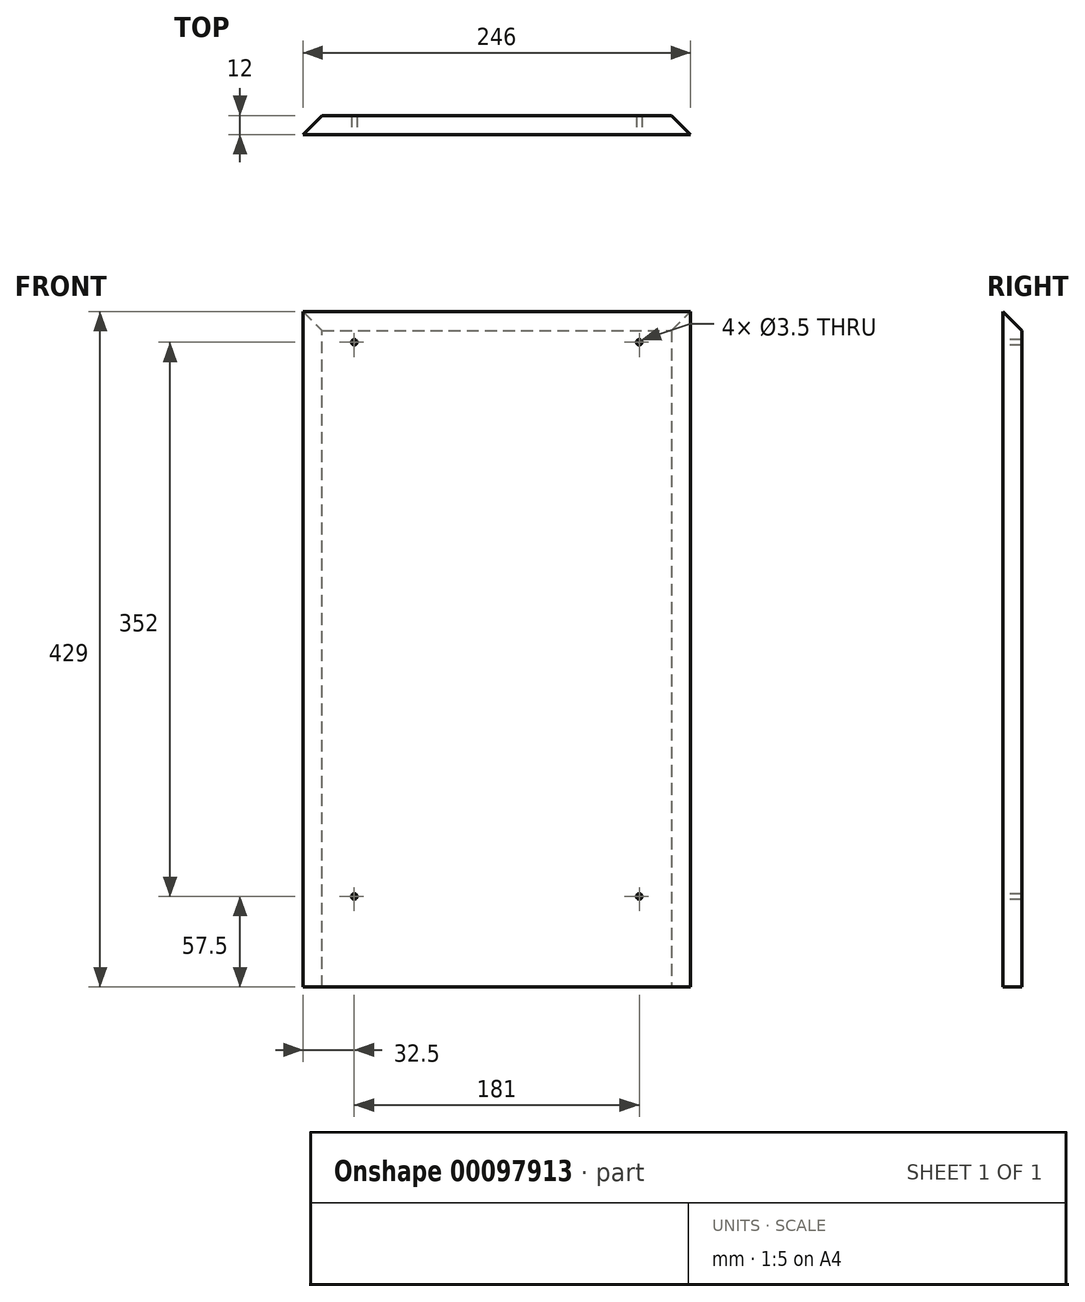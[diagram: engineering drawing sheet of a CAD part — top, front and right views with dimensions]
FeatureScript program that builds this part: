
annotation { "Feature Type Name" : "Feature", "Feature Type Description" : "" }
export const myFeature = defineFeature(function(context is Context, id is Id, definition is map)
    precondition{}
    {
        {
            var Q0;
            Q0=qCreatedBy(makeId("Front.planeOp"),FACE);
            var sketch = newSketch(context, id + "F0", { "sketchPlane" : qUnion([Q0])});
            skLineSegment(sketch, "E0.bottom", {"start": v(-123, 214.5) * mm, "end": v(123, 214.5) * mm});
            skLineSegment(sketch, "E0.top", {"start": v(-123, -214.5) * mm, "end": v(123, -214.5) * mm});
            skLineSegment(sketch, "E0.left", {"start": v(-123, 214.5) * mm, "end": v(-123, -214.5) * mm});
            skLineSegment(sketch, "E0.right", {"start": v(123, 214.5) * mm, "end": v(123, -214.5) * mm});
            skSolve(sketch);
        }
        {
            var Q0;
            Q0=makeQuery(id+"F0.imprint","IMPRINT",FACE,{"disambiguationData":[TD([[makeQuery(id+"F0.imprint","IMPRINT",EDGE,{"derivedFrom":sQuery(id+"F0.wireOp",EDGE,"E0.bottom")}),-1.0]])]});
            extrude(context, id + "F1", {"entities" : qUnion([Q0]), "depth" : 12 * mm});
        }
        {
            var Q0;
            Q0=makeQuery(id+"F1.opExtrude","CAP_EDGE",EDGE,{"disambiguationData":[OSD([sQuery(id+"F0.wireOp",EDGE,"E0.right")])],"isStart":true});
            var Q1;
            Q1=makeQuery(id+"F1.opExtrude","CAP_EDGE",EDGE,{"disambiguationData":[OSD([sQuery(id+"F0.wireOp",EDGE,"E0.bottom")])],"isStart":true});
            var Q2;
            Q2=makeQuery(id+"F1.opExtrude","CAP_EDGE",EDGE,{"disambiguationData":[OSD([sQuery(id+"F0.wireOp",EDGE,"E0.left")])],"isStart":true});
            chamfer(context, id + "F2", {"entities" : qUnion([Q0, Q1, Q2]), "width" : 12 * mm, "tangentPropagation" : true});
        }
        {
            var Q0;
            Q0=makeQuery(id+"F1.opExtrude","CAP_FACE",FACE,{"disambiguationData":[OSD([sQuery(id+"F0.wireOp",EDGE,"E0.bottom"),sQuery(id+"F0.wireOp",EDGE,"E0.top"),sQuery(id+"F0.wireOp",EDGE,"E0.left"),sQuery(id+"F0.wireOp",EDGE,"E0.right")])],"isStart":false});
            var sketch = newSketch(context, id + "F3", { "sketchPlane" : qUnion([Q0])});
            skLineSegment(sketch, "E1.0", {"start": v(-103.5, 195) * mm, "end": v(-103.5, -195) * mm, "construction": true});
            skLineSegment(sketch, "E1.1", {"start": v(103.5, 195) * mm, "end": v(-103.5, 195) * mm, "construction": true});
            skLineSegment(sketch, "E1.2", {"start": v(103.5, -195) * mm, "end": v(103.5, 195) * mm, "construction": true});
            skLineSegment(sketch, "E1.3", {"start": v(-103.5, -195) * mm, "end": v(103.5, -195) * mm, "construction": true});
            skLineSegment(sketch, "E2.0", {"start": v(-90.5, 182) * mm, "end": v(-90.5, -182) * mm, "construction": true});
            skLineSegment(sketch, "E2.1", {"start": v(90.5, 182) * mm, "end": v(-90.5, 182) * mm, "construction": true});
            skLineSegment(sketch, "E2.2", {"start": v(90.5, -182) * mm, "end": v(90.5, 182) * mm, "construction": true});
            skLineSegment(sketch, "E2.3", {"start": v(-90.5, -182) * mm, "end": v(90.5, -182) * mm, "construction": true});
            skPoint(sketch, "E3", {"position": v(-90.5, 195) * mm});
            skPoint(sketch, "E4", {"position": v(90.5, 195) * mm});
            skLineSegment(sketch, "E5", {"start": v(-90.5, -157) * mm, "end": v(90.5, -157) * mm, "construction": true});
            skSolve(sketch);
        }
        {
            var Q0;
            Q0=sQuery(id+"F3.wireOp",VERTEX,"e5c16d88-babf-4eeb-86cf-c37d305e2a05");
            var Q1;
            Q1=sQuery(id+"F3.wireOp",VERTEX,"E3");
            var Q2;
            Q2=sQuery(id+"F3.wireOp",VERTEX,"E4");
            var Q3;
            Q3=sQuery(id+"F3.wireOp",VERTEX,"c294102d-54f9-4299-ab87-e131a3e93fb8");
            var Q4;
            Q4=sQuery(id+"F3.wireOp",VERTEX,"106ebecb-0b84-4ecd-a8f3-c7cece20bac7");
            var Q5;
            Q5=sQuery(id+"F3.wireOp",VERTEX,"a69b0dfd-2533-4f85-9b50-ba4e653f2e6b");
            var Q6;
            Q6=sQuery(id+"F3.wireOp",VERTEX,"e281a5cd-4b1b-4e26-b3f3-f841a09d61fd");
            var Q7;
            Q7=sQuery(id+"F3.wireOp",VERTEX,"dfd3bfd7-63fc-4097-978d-625fc51288cd");
            var Q8;
            Q8=sQuery(id+"F3.wireOp",VERTEX,"W5Vad0r7-cgHH-nYx1-sDlv-v1QaZr2DX3jY.start");
            var Q9;
            Q9=sQuery(id+"F3.wireOp",VERTEX,"W5Vad0r7-cgHH-nYx1-sDlv-v1QaZr2DX3jY.end");
            var Q10;
            Q10=sQuery(id+"F3.wireOp",VERTEX,"E5.start");
            var Q11;
            Q11=sQuery(id+"F3.wireOp",VERTEX,"E5.end");
            var Q12;
            Q12=makeQuery(id+"F1.opExtrude","SWEPT_BODY",BODY,{"disambiguationData":[OSD([sQuery(id+"F0.wireOp",EDGE,"E0.bottom"),sQuery(id+"F0.wireOp",EDGE,"E0.top"),sQuery(id+"F0.wireOp",EDGE,"E0.left"),sQuery(id+"F0.wireOp",EDGE,"E0.right")])]});
            hole(context, id + "F4", {"style" : HoleStyle.SIMPLE, "endStyle" : HoleEndStyle.THROUGH, "holeDiameter" : 3.5 * mm, "locations" : qUnion([Q0, Q1, Q2, Q3, Q4, Q5, Q6, Q7, Q8, Q9, Q10, Q11]), "scope" : qUnion([Q12]), "isTappedThrough" : true});
        }
    });
